# Revit family: Torno Stool
name_source: partatom
category: Furniture
revit_build: Autodesk Revit 2017 (Build: 20171027_0315(x64)
units: mm (PartAtom-declared; Revit-internal decimal feet)

## family parameters
Always vertical = Yes
Cut with Voids When Loaded = No
OmniClass Number = 23.40.20.00
OmniClass Title = General Furniture and Specialties
Room Calculation Point = No
Shared = No
Work Plane-Based = No

## types (1)
- Torno Stool
    Accessories = Cushion Ø38
    Depth (cm) = 50
    Depth (in) = 19,7
    Designer = Form Us With Love
    Feet = +Halle Pom - black
    Flame resistance BS = Foam BS5852 crib 5 certified (US does not apply)
    Frame = +Halle Powdercoated aluminium - RAL 6028
    Height (cm) = 45
    Height (in) = 17,7
    Packaging Dimensions (cm) = 44 / 43 / 47
    Packaging Dimensions (in) = 17.32 / 16.93 / 18.50
    Product family = Torno
    Seating Height (cm) = 45
    Seating Height (in) = 17,7
    URL = https://www.plushalle.com
    Variations = Optional upholstered seat. Available in all fabrics and leather types.
    Warranty period = 2 years standard warranty
    Weight (kg) = 5,5
    Weight (lbs) = 12,1
    Width (cm) = 50
    Width (in) = 19,7

## geometry (parser evidence)
native form markers: Sweep x2
no freeform markers — native parametric forms only
